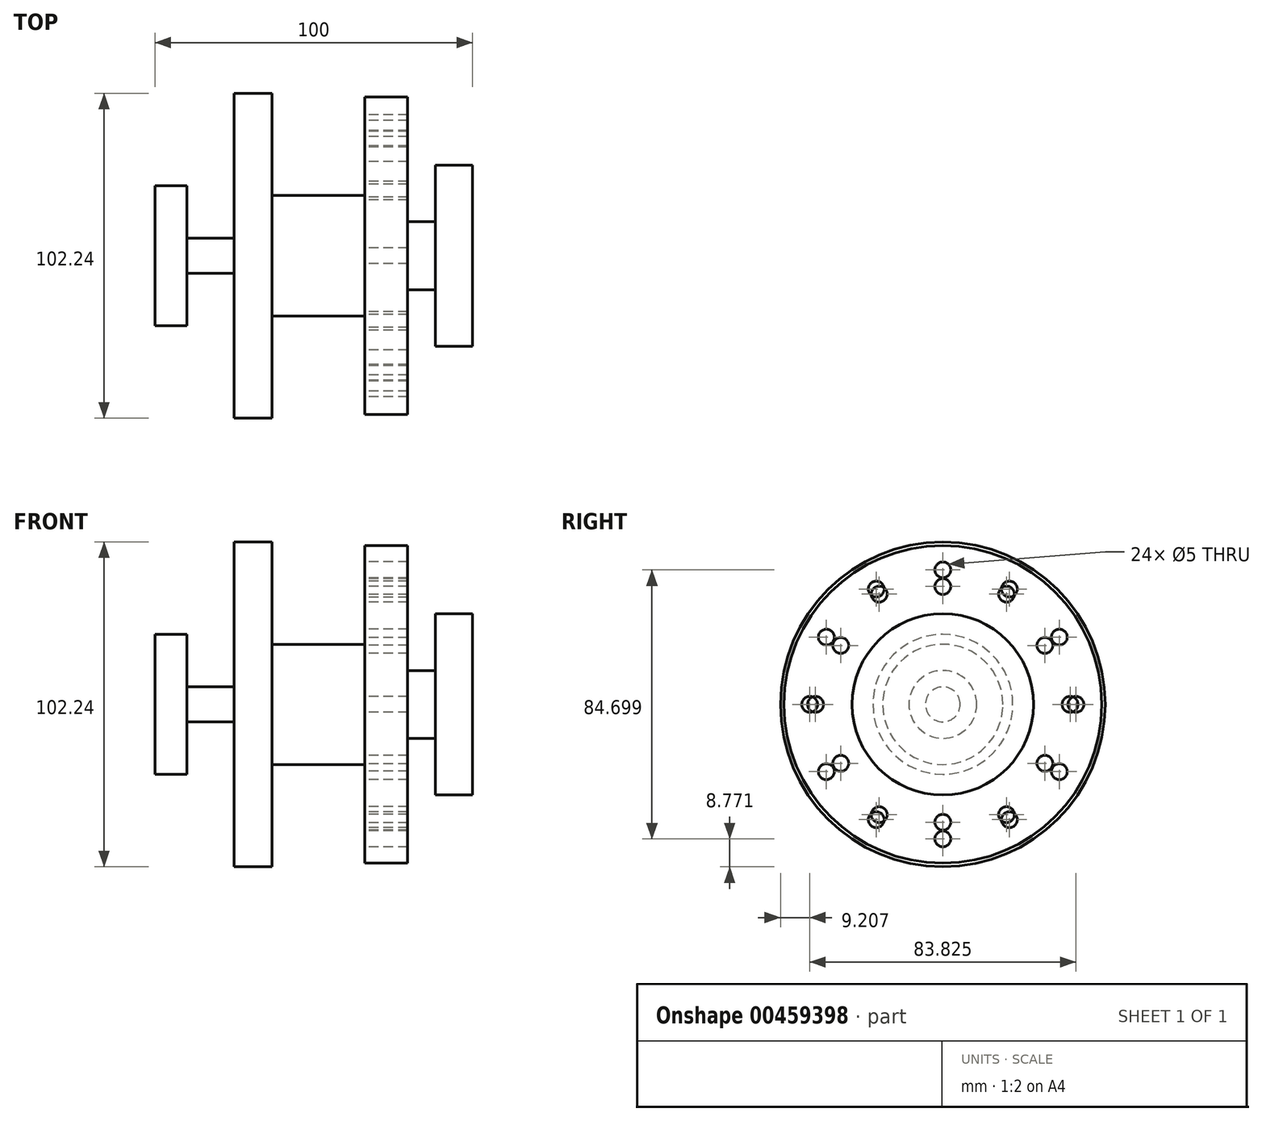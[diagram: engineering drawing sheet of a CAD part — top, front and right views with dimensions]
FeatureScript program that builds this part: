
annotation { "Feature Type Name" : "Feature", "Feature Type Description" : "" }
export const myFeature = defineFeature(function(context is Context, id is Id, definition is map)
    precondition{}
    {
        {
            var Q0;
            Q0=qCreatedBy(makeId("Front.planeOp"),FACE);
            var sketch = newSketch(context, id + "F0", { "sketchPlane" : qUnion([Q0])});
            skLineSegment(sketch, "E0", {"start": v(-45.72, 0) * mm, "end": v(-45.72, 22.02) * mm});
            skLineSegment(sketch, "E1", {"start": v(-45.72, 22.02) * mm, "end": v(-35.61, 22.02) * mm});
            skLineSegment(sketch, "E2", {"start": v(-35.61, 22.02) * mm, "end": v(-35.61, 5.5) * mm});
            skLineSegment(sketch, "E3", {"start": v(-35.61, 5.5) * mm, "end": v(-20.82, 5.5) * mm});
            skLineSegment(sketch, "E4", {"start": v(-20.82, 5.5) * mm, "end": v(-20.82, 51.12) * mm});
            skLineSegment(sketch, "E5", {"start": v(-20.82, 51.12) * mm, "end": v(-8.82, 51.12) * mm});
            skLineSegment(sketch, "E6", {"start": v(-8.82, 51.12) * mm, "end": v(-8.82, 18.94) * mm});
            skLineSegment(sketch, "E7", {"start": v(-8.82, 18.94) * mm, "end": v(20.4, 18.94) * mm});
            skLineSegment(sketch, "E8", {"start": v(20.4, 18.94) * mm, "end": v(20.4, 50.01) * mm});
            skLineSegment(sketch, "E9", {"start": v(20.4, 50.01) * mm, "end": v(33.85, 50.01) * mm});
            skLineSegment(sketch, "E10", {"start": v(33.85, 50.01) * mm, "end": v(33.85, 10.68) * mm});
            skLineSegment(sketch, "E11", {"start": v(33.85, 10.68) * mm, "end": v(42.6, 10.68) * mm});
            skLineSegment(sketch, "E12", {"start": v(42.6, 10.68) * mm, "end": v(42.6, 28.56) * mm});
            skLineSegment(sketch, "E13", {"start": v(42.6, 28.56) * mm, "end": v(54.28, 28.56) * mm});
            skLineSegment(sketch, "E14", {"start": v(54.28, 28.56) * mm, "end": v(54.28, 0) * mm});
            skLineSegment(sketch, "E15", {"start": v(54.28, 0) * mm, "end": v(-45.72, 0) * mm});
            skSolve(sketch);
        }
        {
            var Q0;
            Q0 = qSketchRegion(id + "F0", true);
            var Q1;
            Q1=sQuery(id+"F0.wireOp",EDGE,"E15");
            revolve(context, id + "F1", {"entities" : qUnion([Q0]), "axis" : qUnion([Q1]), "revolveType" : RevolveType.FULL});
        }
        {
            var Q0;
            Q0=qCreatedBy(makeId("Right.planeOp"),FACE);
            var sketch = newSketch(context, id + "F2", { "sketchPlane" : qUnion([Q0])});
            skPoint(sketch, "E16", {"position": v(0, 37.1) * mm});
            skPoint(sketch, "E17", {"position": v(0, -42.35) * mm});
            skPoint(sketch, "E18", {"position": v(40.08, 0) * mm});
            skPoint(sketch, "E19", {"position": v(-41.91, 0) * mm});
            skSolve(sketch);
        }
        {
            var Q0;
            Q0=sQuery(id+"F2.wireOp",VERTEX,"E16");
            var Q1;
            Q1=sQuery(id+"F2.wireOp",VERTEX,"E18");
            var Q2;
            Q2=sQuery(id+"F2.wireOp",VERTEX,"E19");
            var Q3;
            Q3=sQuery(id+"F2.wireOp",VERTEX,"E17");
            var Q4;
            Q4=makeQuery(id+"F1.opRevolve","SWEPT_BODY",BODY,{"disambiguationData":[OSD([sQuery(id+"F0.wireOp",EDGE,"E0"),sQuery(id+"F0.wireOp",EDGE,"E1"),sQuery(id+"F0.wireOp",EDGE,"E2"),sQuery(id+"F0.wireOp",EDGE,"E3"),sQuery(id+"F0.wireOp",EDGE,"E4"),sQuery(id+"F0.wireOp",EDGE,"E5"),sQuery(id+"F0.wireOp",EDGE,"E6"),sQuery(id+"F0.wireOp",EDGE,"E7"),sQuery(id+"F0.wireOp",EDGE,"E8"),sQuery(id+"F0.wireOp",EDGE,"E9"),sQuery(id+"F0.wireOp",EDGE,"E10"),sQuery(id+"F0.wireOp",EDGE,"E11"),sQuery(id+"F0.wireOp",EDGE,"E12"),sQuery(id+"F0.wireOp",EDGE,"E13"),sQuery(id+"F0.wireOp",EDGE,"E14"),sQuery(id+"F0.wireOp",EDGE,"E15")])]});
            hole(context, id + "F3", {"style" : HoleStyle.SIMPLE, "endStyle" : HoleEndStyle.THROUGH, "oppositeDirection" : true, "holeDiameter" : 5 * mm, "isTappedThrough" : true, "tappedDepth" : 12 * mm, "tapClearance" : 3, "locations" : qUnion([Q0, Q1, Q2, Q3]), "scope" : qUnion([Q4])});
        }
        {
            var Q0;
            Q0=makeQuery(id+"F1.opRevolve","SWEPT_BODY",BODY,{"disambiguationData":[OSD([sQuery(id+"F0.wireOp",EDGE,"E0"),sQuery(id+"F0.wireOp",EDGE,"E1"),sQuery(id+"F0.wireOp",EDGE,"E2"),sQuery(id+"F0.wireOp",EDGE,"E3"),sQuery(id+"F0.wireOp",EDGE,"E4"),sQuery(id+"F0.wireOp",EDGE,"E5"),sQuery(id+"F0.wireOp",EDGE,"E6"),sQuery(id+"F0.wireOp",EDGE,"E7"),sQuery(id+"F0.wireOp",EDGE,"E8"),sQuery(id+"F0.wireOp",EDGE,"E9"),sQuery(id+"F0.wireOp",EDGE,"E10"),sQuery(id+"F0.wireOp",EDGE,"E11"),sQuery(id+"F0.wireOp",EDGE,"E12"),sQuery(id+"F0.wireOp",EDGE,"E13"),sQuery(id+"F0.wireOp",EDGE,"E14"),sQuery(id+"F0.wireOp",EDGE,"E15")])]});
            var Q1;
            Q1=makeQuery(id+"F1.opRevolve","SWEPT_EDGE",EDGE,{"disambiguationData":[OSD([sQuery(id+"F0.wireOp",EDGE,"E4"),sQuery(id+"F0.wireOp",EDGE,"E5")])]});
            circularPattern(context, id + "F4", {"entities" : qUnion([Q0]), "axis" : qUnion([Q1]), "angle" : 360 * degree, "instanceCount" : 6, "equalSpace" : true});
        }
    });
